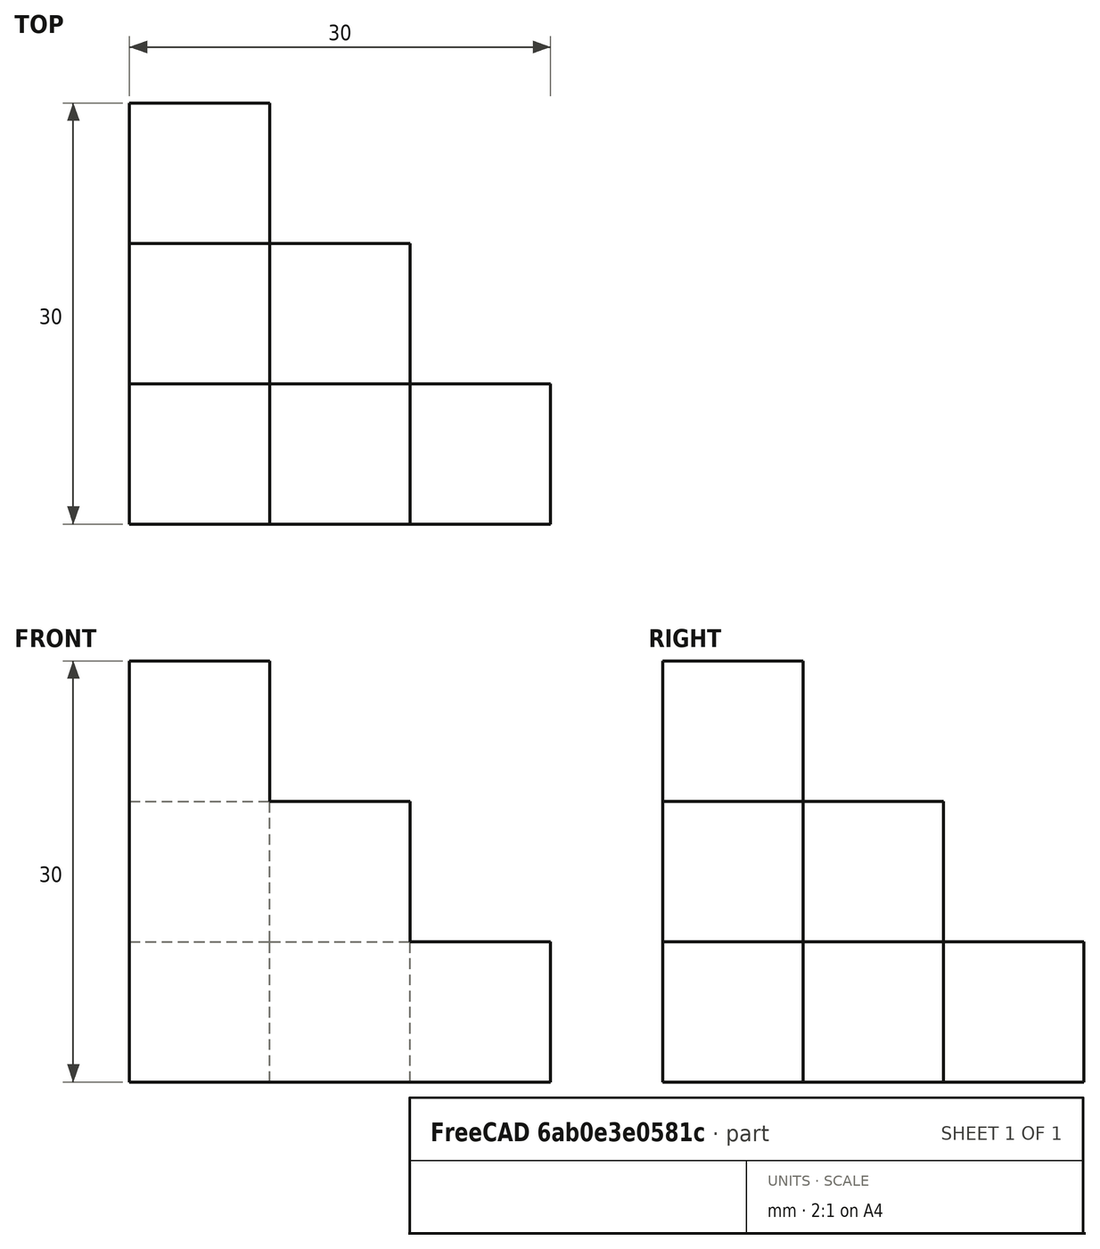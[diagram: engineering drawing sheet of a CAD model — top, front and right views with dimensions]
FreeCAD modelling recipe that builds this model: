
FCSTD DOCUMENT  (FreeCAD 0.21R33694 (Git))
Label: OJT1_T05R04_fusion-qubert3
License: All rights reserved
LicenseURL: http://en.wikipedia.org/wiki/All_rights_reserved
objects: Part::Box×6, Part::MultiFuse×1
note: 7 computed .brp shape members not serialized (recipe doc carries the construction recipe); baked Part::Feature solids carry a one-line shape summary decoded from their .brp

FEATURE [Part::Box] Box  label="cubo1"
  AttacherType = Attacher::AttachEngine3D
  Height = 30
  Length = 10
  Width = 10
FEATURE [Part::Box] Box001  label="cubo2"
  AttacherType = Attacher::AttachEngine3D
  Height = 20
  Length = 10
  Placement = pos=(10,0,0) rot=(0,0,1;0rad)
  Width = 10
FEATURE [Part::Box] Box002  label="cubo3"
  AttacherType = Attacher::AttachEngine3D
  Height = 20
  Length = 10
  Placement = pos=(0,10,0) rot=(0,0,1;0rad)
  Width = 10
FEATURE [Part::Box] Box003  label="cubo4"
  AttacherType = Attacher::AttachEngine3D
  Height = 10
  Length = 10
  Placement = pos=(20,0,0) rot=(0,0,1;0rad)
  Width = 10
FEATURE [Part::Box] Box004  label="cubo5"
  AttacherType = Attacher::AttachEngine3D
  Height = 10
  Length = 10
  Placement = pos=(0,20,0) rot=(0,0,1;0rad)
  Width = 10
FEATURE [Part::Box] Box005  label="cubo6"
  AttacherType = Attacher::AttachEngine3D
  Height = 10
  Length = 10
  Placement = pos=(10,10,0) rot=(0,0,1;0rad)
  Width = 10
FEATURE [Part::MultiFuse] Fusion
  Refine = true
  Shapes = -> [Box,Box001,Box002,Box003,Box004,Box005]
